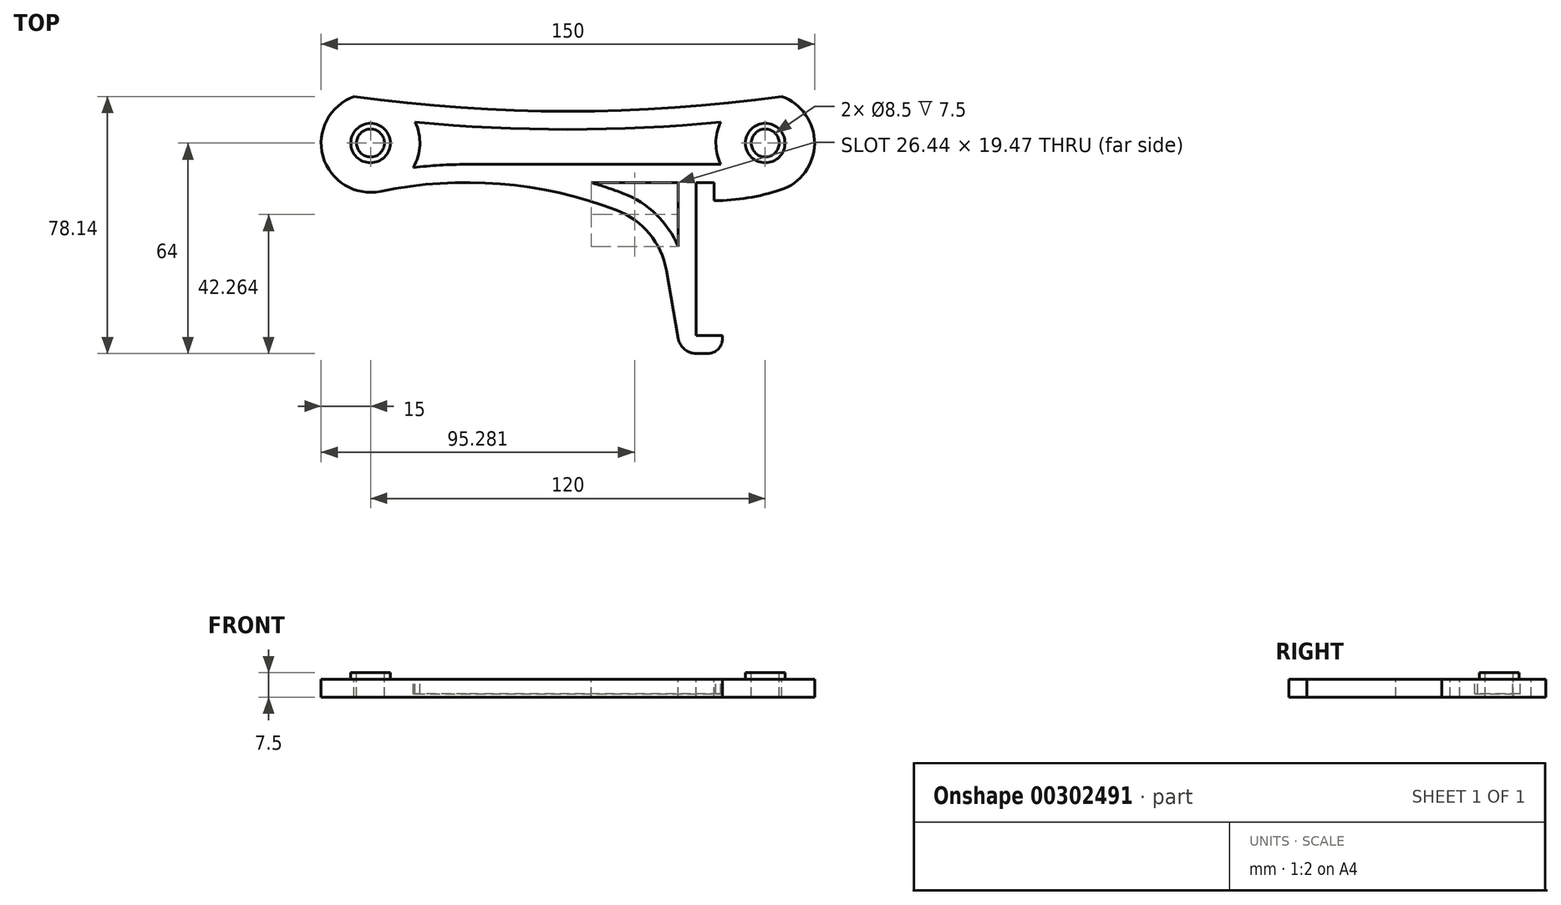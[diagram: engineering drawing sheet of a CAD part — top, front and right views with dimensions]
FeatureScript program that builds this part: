
annotation { "Feature Type Name" : "Feature", "Feature Type Description" : "" }
export const myFeature = defineFeature(function(context is Context, id is Id, definition is map)
    precondition{}
    {
        {
            var Q0;
            Q0=qCreatedBy(makeId("Top.planeOp"),FACE);
            var sketch = newSketch(context, id + "F0", { "sketchPlane" : qUnion([Q0])});
            skCircle(sketch, "E0", {"center": v(21, 12) * mm, "radius": 4.25 * mm});
            skCircle(sketch, "E1", {"center": v(-99, 12) * mm, "radius": 4.25 * mm});
            skCircle(sketch, "E2", {"center": v(21, 12) * mm, "radius": 6 * mm});
            skCircle(sketch, "E3", {"center": v(-99, 12) * mm, "radius": 6 * mm});
            skArc(sketch, "E4", {"start": v(25.68, -2.25) * mm, "mid": v(36, 11.83) * mm, "end": v(26, 26.14) * mm});
            skArc(sketch, "E5", {"start": v(-104, 26.14) * mm, "mid": v(-113.45, 7.96) * mm, "end": v(-95.94, -2.69) * mm});
            skArc(sketch, "E6", {"start": v(-104, 26.14) * mm, "mid": v(-39, 21.64) * mm, "end": v(26, 26.14) * mm});
            skLineSegment(sketch, "E7", {"start": v(-99, 12) * mm, "end": v(21, 12) * mm, "construction": true});
            skLineSegment(sketch, "E8", {"start": v(-39, 21.64) * mm, "end": v(-39, -3.78) * mm, "construction": true});
            skPoint(sketch, "E8.startSnap0", {"position": v(-39, 21.64) * mm});
            skPoint(sketch, "E8.endSnap0", {"position": v(-39, 12) * mm});
            skLineSegment(sketch, "E9", {"start": v(-9.08, -26.7) * mm, "end": v(-5.42, -47.46) * mm});
            skLineSegment(sketch, "E10", {"start": v(0, -52) * mm, "end": v(3.5, -52) * mm});
            skLineSegment(sketch, "E11", {"start": v(8, -47.5) * mm, "end": v(8, -46.5) * mm});
            skLineSegment(sketch, "E12", {"start": v(8, -46.5) * mm, "end": v(0, -46.5) * mm});
            skLineSegment(sketch, "E13", {"start": v(0, -46.5) * mm, "end": v(0, 0) * mm});
            skLineSegment(sketch, "E14", {"start": v(0, 0) * mm, "end": v(5.5, 0) * mm});
            skLineSegment(sketch, "E15", {"start": v(5.5, 0) * mm, "end": v(5.5, -5.5) * mm});
            skArc(sketch, "E16", {"start": v(-24.14, -8.44) * mm, "mid": v(-59.63, -0.4) * mm, "end": v(-95.94, -2.69) * mm});
            skArc(sketch, "E17", {"start": v(-9.08, -26.7) * mm, "mid": v(-14.2, -15.58) * mm, "end": v(-24.14, -8.44) * mm});
            skArc(sketch, "E18.filletArc", {"start": v(-5.42, -47.46) * mm, "mid": v(-3.54, -50.71) * mm, "end": v(0, -52) * mm});
            skLineSegment(sketch, "E19", {"start": v(0, 0) * mm, "end": v(-90, 0) * mm, "construction": true});
            skArc(sketch, "E20", {"start": v(5.5, -5.5) * mm, "mid": v(15.72, -4.67) * mm, "end": v(25.68, -2.25) * mm});
            skArc(sketch, "E21.filletArc", {"start": v(3.5, -52) * mm, "mid": v(6.68, -50.68) * mm, "end": v(8, -47.5) * mm});
            skArc(sketch, "E22", {"start": v(-86, 4.52) * mm, "mid": v(-84.01, 11.4) * mm, "end": v(-85.44, 18.4) * mm});
            skArc(sketch, "E23", {"start": v(7.44, 18.4) * mm, "mid": v(6, 11.95) * mm, "end": v(7.48, 5.5) * mm});
            skArc(sketch, "E24", {"start": v(-85.44, 18.4) * mm, "mid": v(-39, 16.14) * mm, "end": v(7.44, 18.4) * mm});
            skArc(sketch, "E25", {"start": v(-22.17, -3.3) * mm, "mid": v(-27.02, -1.56) * mm, "end": v(-31.94, 0) * mm});
            skLineSegment(sketch, "E26.2", {"start": v(-5.5, -19.47) * mm, "end": v(-5.5, 0) * mm});
            skLineSegment(sketch, "E27", {"start": v(7.48, 5.5) * mm, "end": v(-69.86, 5.5) * mm});
            skLineSegment(sketch, "E28", {"start": v(-5.5, 0) * mm, "end": v(-31.94, 0) * mm});
            skArc(sketch, "E29.trimOffspring", {"start": v(-69.86, 5.5) * mm, "mid": v(-77.94, 5.26) * mm, "end": v(-86, 4.52) * mm});
            skArc(sketch, "E30.0", {"start": v(-5.5, -19.47) * mm, "mid": v(-12.18, -9.68) * mm, "end": v(-22.17, -3.3) * mm});
            skSolve(sketch);
        }
        {
            var Q0;
            Q0=makeQuery(id+"F0.imprint","IMPRINT",FACE,{"disambiguationData":[TD([[makeQuery(id+"F0.imprint","IMPRINT",EDGE,{"derivedFrom":sQuery(id+"F0.wireOp",EDGE,"E2")}),-1.0]])]});
            var Q1;
            Q1=makeQuery(id+"F0.imprint","IMPRINT",FACE,{"disambiguationData":[TD([[makeQuery(id+"F0.imprint","IMPRINT",EDGE,{"derivedFrom":sQuery(id+"F0.wireOp",EDGE,"E0")}),-1.0]])]});
            var Q2;
            Q2=makeQuery(id+"F0.imprint","IMPRINT",FACE,{"disambiguationData":[TD([[makeQuery(id+"F0.imprint","IMPRINT",EDGE,{"derivedFrom":sQuery(id+"F0.wireOp",EDGE,"E1")}),-1.0]])]});
            extrude(context, id + "F1", {"entities" : qUnion([Q0, Q1, Q2]), "oppositeDirection" : true, "depth" : 5.5 * mm});
        }
        {
            var Q0;
            Q0=makeQuery(id+"F0.imprint","IMPRINT",FACE,{"disambiguationData":[TD([[makeQuery(id+"F0.imprint","IMPRINT",EDGE,{"derivedFrom":sQuery(id+"F0.wireOp",EDGE,"E0")}),-1.0]])]});
            var Q1;
            Q1=makeQuery(id+"F0.imprint","IMPRINT",FACE,{"disambiguationData":[TD([[makeQuery(id+"F0.imprint","IMPRINT",EDGE,{"derivedFrom":sQuery(id+"F0.wireOp",EDGE,"E1")}),-1.0]])]});
            extrude(context, id + "F2", {"entities" : qUnion([Q0, Q1]), "operationType" : NewBodyOperationType.ADD, "depth" : 2 * mm});
        }
        {
            var Q0;
            Q0=makeQuery(id+"F0.imprint","IMPRINT",FACE,{"disambiguationData":[TD([[makeQuery(id+"F0.imprint","IMPRINT",EDGE,{"derivedFrom":sQuery(id+"F0.wireOp",EDGE,"E22")}),-1.0]])]});
            var Q1;
            Q1=makeQuery(id+"F1.opExtrude","CAP_VERTEX",VERTEX,{"disambiguationData":[OSD([sQuery(id+"F0.wireOp",EDGE,"E5"),sQuery(id+"F0.wireOp",EDGE,"E16")])],"isStart":false});
            extrude(context, id + "F3", {"entities" : qUnion([Q0]), "operationType" : NewBodyOperationType.ADD, "endBound" : BoundingType.UP_TO_VERTEX, "oppositeDirection" : true, "endBoundEntityVertex" : qUnion([Q1]), "depth" : 3 * mm, "hasSecondDirection" : true, "secondDirectionOppositeDirection" : true, "secondDirectionDepth" : 4.5 * mm});
        }
    });
